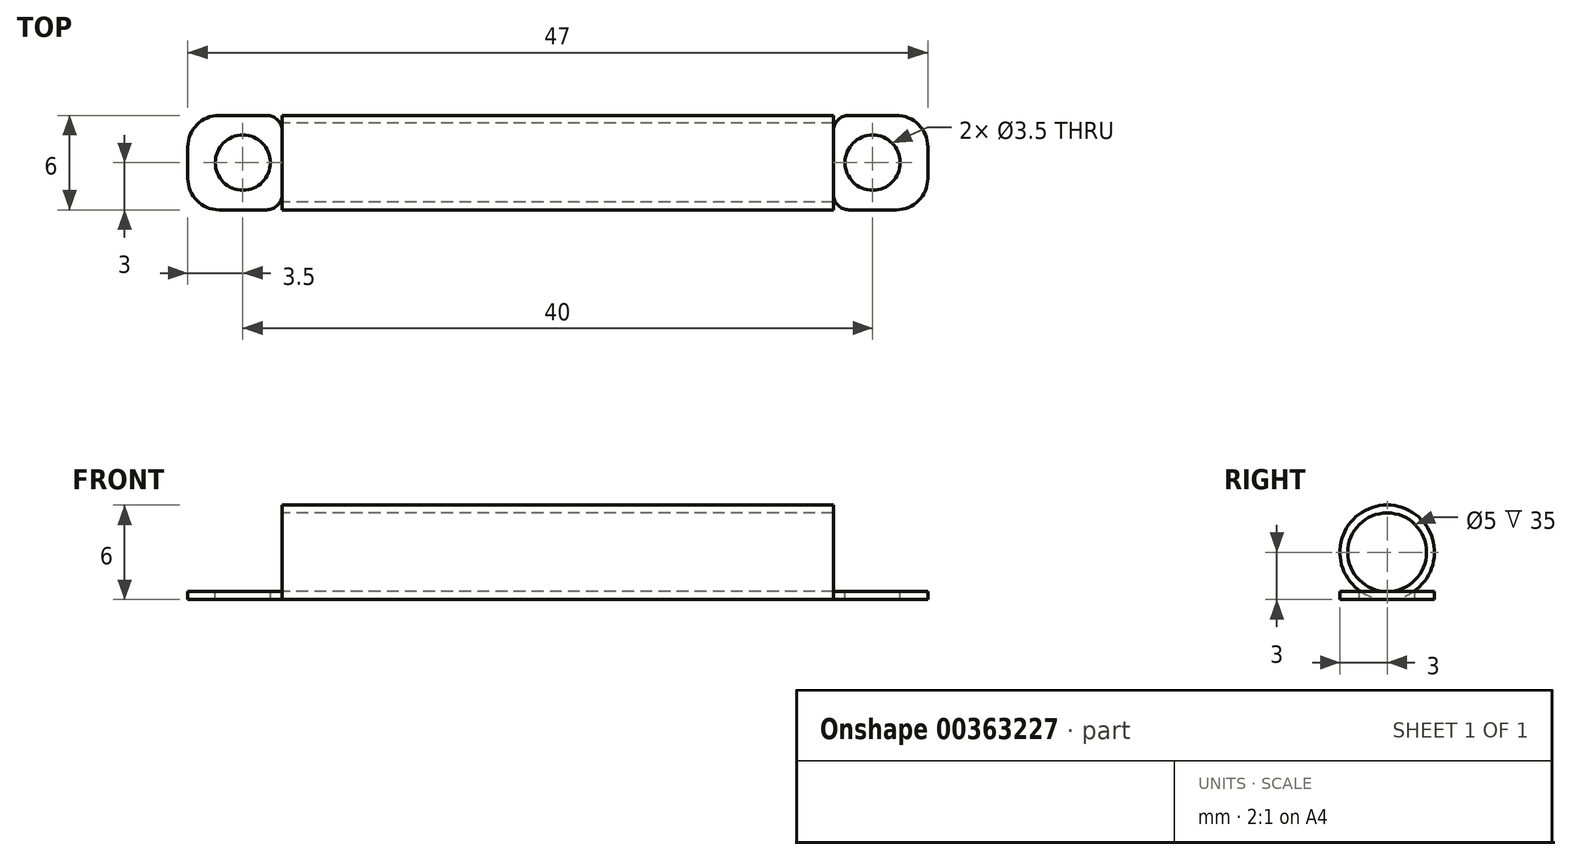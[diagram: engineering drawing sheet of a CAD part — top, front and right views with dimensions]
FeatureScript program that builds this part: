
annotation { "Feature Type Name" : "Feature", "Feature Type Description" : "" }
export const myFeature = defineFeature(function(context is Context, id is Id, definition is map)
    precondition{}
    {
        {
            var Q0;
            Q0=qCreatedBy(makeId("Right.planeOp"),FACE);
            var sketch = newSketch(context, id + "F0", { "sketchPlane" : qUnion([Q0])});
            skCircle(sketch, "E0", {"center": v(0, 0) * mm, "radius": 3 * mm});
            skCircle(sketch, "E1.0", {"center": v(0, 0) * mm, "radius": 2.5 * mm});
            skSolve(sketch);
        }
        {
            var Q0;
            Q0=makeQuery(id+"F0.imprint","IMPRINT",FACE,{"disambiguationData":[TD([[makeQuery(id+"F0.imprint","IMPRINT",EDGE,{"derivedFrom":sQuery(id+"F0.wireOp",EDGE,"E0")}),1.0]])]});
            extrude(context, id + "F1", {"entities" : qUnion([Q0]), "endBound" : BoundingType.SYMMETRIC, "depth" : 35 * mm});
        }
        {
            var Q0;
            Q0=qCreatedBy(makeId("Top.planeOp"),FACE);
            cPlane(context, id + "F2", {"entities" : qUnion([Q0]), "cplaneType" : CPlaneType.OFFSET, "offset" : 3 * mm, "oppositeDirection" : true, "width" : 150 * mm, "height" : 150 * mm});
        }
        {
            var Q0;
            Q0=qCreatedBy(id+"F2.planeOp",FACE);
            var sketch = newSketch(context, id + "F3", { "sketchPlane" : qUnion([Q0])});
            skLineSegment(sketch, "E2", {"start": v(-17.5, 3) * mm, "end": v(17.5, 3) * mm});
            skLineSegment(sketch, "E3", {"start": v(17.5, -3) * mm, "end": v(-17.5, -3) * mm});
            skLineSegment(sketch, "E4.bottom", {"start": v(17.5, 3) * mm, "end": v(23.5, 3) * mm});
            skLineSegment(sketch, "E4.top", {"start": v(17.5, -3) * mm, "end": v(23.5, -3) * mm});
            skLineSegment(sketch, "E4.left", {"start": v(17.5, 3) * mm, "end": v(17.5, -3) * mm});
            skLineSegment(sketch, "E4.right", {"start": v(23.5, 3) * mm, "end": v(23.5, -3) * mm});
            skLineSegment(sketch, "E5.bottom", {"start": v(-17.5, 3) * mm, "end": v(-23.5, 3) * mm});
            skLineSegment(sketch, "E5.top", {"start": v(-17.5, -3) * mm, "end": v(-23.5, -3) * mm});
            skLineSegment(sketch, "E5.left", {"start": v(-17.5, 3) * mm, "end": v(-17.5, -3) * mm});
            skLineSegment(sketch, "E5.right", {"start": v(-23.5, 3) * mm, "end": v(-23.5, -3) * mm});
            skSolve(sketch);
        }
        {
            var Q0;
            Q0=makeQuery(id+"F3.imprint","IMPRINT",FACE,{"disambiguationData":[TD([[makeQuery(id+"F3.imprint","IMPRINT",EDGE,{"derivedFrom":sQuery(id+"F3.wireOp",EDGE,"E4.bottom")}),-1.0]])]});
            var Q1;
            Q1=makeQuery(id+"F3.imprint","IMPRINT",FACE,{"disambiguationData":[TD([[makeQuery(id+"F3.imprint","IMPRINT",EDGE,{"derivedFrom":sQuery(id+"F3.wireOp",EDGE,"E5.bottom")}),1.0]])]});
            extrude(context, id + "F4", {"entities" : qUnion([Q0, Q1]), "operationType" : NewBodyOperationType.ADD, "depth" : .5 * mm});
        }
        {
            var Q0;
            Q0=makeQuery(id+"F4.opExtrude","CAP_FACE",FACE,{"disambiguationData":[OSD([sQuery(id+"F3.wireOp",EDGE,"E4.bottom"),sQuery(id+"F3.wireOp",EDGE,"E4.top"),sQuery(id+"F3.wireOp",EDGE,"E4.left"),sQuery(id+"F3.wireOp",EDGE,"E4.right")])],"isStart":false});
            var sketch = newSketch(context, id + "F5", { "sketchPlane" : qUnion([Q0])});
            skCircle(sketch, "E6", {"center": v(20, 0) * mm, "radius": 1.75 * mm});
            skPoint(sketch, "E6.centerSnap0", {"position": v(23.5, 0) * mm});
            skPoint(sketch, "E6.centerSnap1", {"position": v(20.5, 3) * mm});
            skLineSegment(sketch, "E7.0.0", {"start": v(-17.5, 1.66) * mm, "end": v(-17.5, 3) * mm});
            skLineSegment(sketch, "E7.0.1", {"start": v(-17.5, 3) * mm, "end": v(-23.5, 3) * mm});
            skLineSegment(sketch, "E7.0.2", {"start": v(-23.5, 3) * mm, "end": v(-23.5, -3) * mm});
            skLineSegment(sketch, "E7.0.3", {"start": v(-23.5, -3) * mm, "end": v(-17.5, -3) * mm});
            skLineSegment(sketch, "E7.0.4", {"start": v(-17.5, -3) * mm, "end": v(-17.5, -1.66) * mm});
            skLineSegment(sketch, "E7.0.5", {"start": v(-17.5, -1.66) * mm, "end": v(-17.5, 0) * mm});
            skLineSegment(sketch, "E7.0.6", {"start": v(-17.5, 0) * mm, "end": v(-17.5, 1.66) * mm});
            skCircle(sketch, "E8", {"center": v(-20, 0) * mm, "radius": 1.75 * mm});
            skPoint(sketch, "E8.centerSnap0", {"position": v(-23.5, 0) * mm});
            skPoint(sketch, "E8.centerSnap1", {"position": v(-20.5, 3) * mm});
            skLineSegment(sketch, "E9", {"start": v(-17.5, 3) * mm, "end": v(17.5, 3) * mm});
            skLineSegment(sketch, "E10", {"start": v(17.5, -3) * mm, "end": v(-17.5, -3) * mm});
            skSolve(sketch);
        }
        {
            var Q0;
            Q0=makeQuery(id+"F4.opExtrude","SWEPT_EDGE",EDGE,{"disambiguationData":[OSD([sQuery(id+"F3.wireOp",EDGE,"E4.bottom"),sQuery(id+"F3.wireOp",EDGE,"E4.right")])]});
            var Q1;
            Q1=makeQuery(id+"F4.opExtrude","SWEPT_EDGE",EDGE,{"disambiguationData":[OSD([sQuery(id+"F3.wireOp",EDGE,"E4.top"),sQuery(id+"F3.wireOp",EDGE,"E4.right")])]});
            var Q2;
            Q2=makeQuery(id+"F4.opExtrude","SWEPT_EDGE",EDGE,{"disambiguationData":[OSD([sQuery(id+"F3.wireOp",EDGE,"E5.top"),sQuery(id+"F3.wireOp",EDGE,"E5.right")])]});
            var Q3;
            Q3=makeQuery(id+"F4.opExtrude","SWEPT_EDGE",EDGE,{"disambiguationData":[OSD([sQuery(id+"F3.wireOp",EDGE,"E5.bottom"),sQuery(id+"F3.wireOp",EDGE,"E5.right")])]});
            fillet(context, id + "F6", {"entities" : qUnion([Q0, Q1, Q2, Q3]), "radius" : 2 * mm, "tangentPropagation" : true, "allowEdgeOverflow" : false});
        }
        {
            var Q0;
            Q0=makeQuery(id+"F4.opExtrude","SWEPT_EDGE",EDGE,{"disambiguationData":[OSD([sQuery(id+"F3.wireOp",EDGE,"E3"),sQuery(id+"F3.wireOp",EDGE,"E4.top"),sQuery(id+"F3.wireOp",EDGE,"E4.left")])]});
            var Q1;
            Q1=makeQuery(id+"F4.opExtrude","SWEPT_EDGE",EDGE,{"disambiguationData":[OSD([sQuery(id+"F3.wireOp",EDGE,"E2"),sQuery(id+"F3.wireOp",EDGE,"E4.bottom"),sQuery(id+"F3.wireOp",EDGE,"E4.left")])]});
            var Q2;
            Q2=makeQuery(id+"F4.opExtrude","SWEPT_EDGE",EDGE,{"disambiguationData":[OSD([sQuery(id+"F3.wireOp",EDGE,"E3"),sQuery(id+"F3.wireOp",EDGE,"E5.top"),sQuery(id+"F3.wireOp",EDGE,"E5.left")])]});
            var Q3;
            Q3=makeQuery(id+"F4.opExtrude","SWEPT_EDGE",EDGE,{"disambiguationData":[OSD([sQuery(id+"F3.wireOp",EDGE,"E2"),sQuery(id+"F3.wireOp",EDGE,"E5.bottom"),sQuery(id+"F3.wireOp",EDGE,"E5.left")])]});
            fillet(context, id + "F7", {"entities" : qUnion([Q0, Q1, Q2, Q3]), "radius" : 1 * mm, "tangentPropagation" : true, "allowEdgeOverflow" : false});
        }
        {
            var Q0;
            Q0=makeQuery(id+"F5.imprint","IMPRINT",FACE,{"disambiguationData":[TD([[makeQuery(id+"F5.imprint","IMPRINT",EDGE,{"derivedFrom":sQuery(id+"F5.wireOp",EDGE,"E6")}),1.0]])]});
            var Q1;
            Q1=makeQuery(id+"F5.imprint","IMPRINT",FACE,{"disambiguationData":[TD([[makeQuery(id+"F5.imprint","IMPRINT",EDGE,{"derivedFrom":sQuery(id+"F5.wireOp",EDGE,"E8")}),1.0]])]});
            extrude(context, id + "F8", {"entities" : qUnion([Q0, Q1]), "operationType" : NewBodyOperationType.REMOVE, "oppositeDirection" : true, "depth" : 25 * mm});
        }
    });
